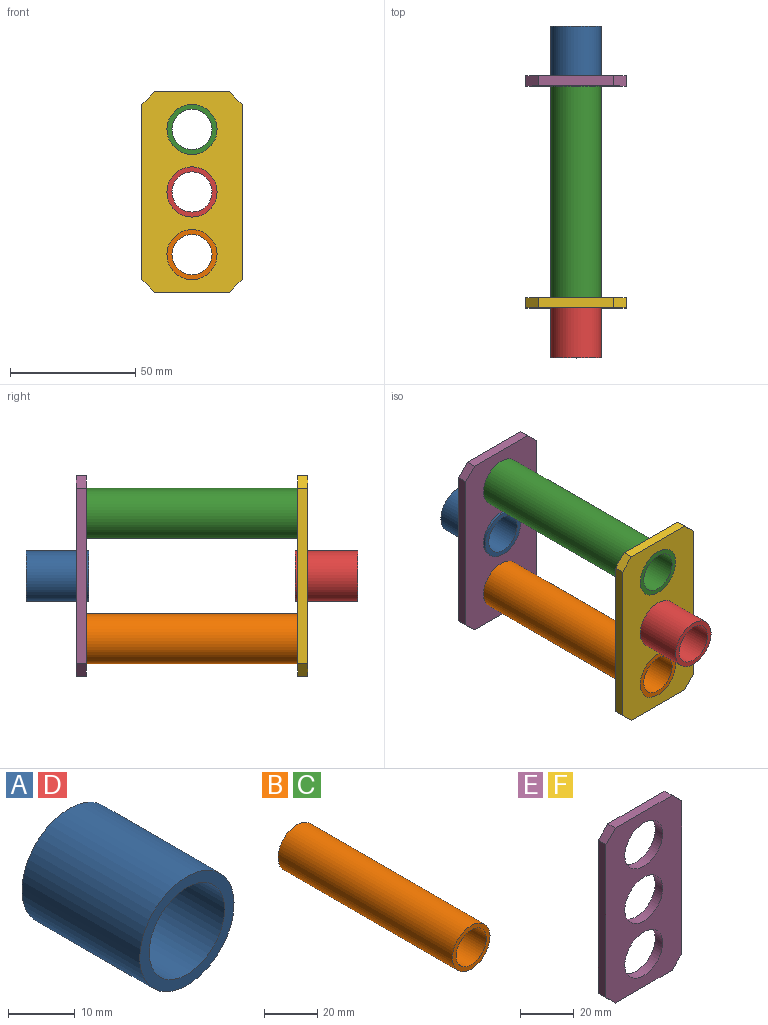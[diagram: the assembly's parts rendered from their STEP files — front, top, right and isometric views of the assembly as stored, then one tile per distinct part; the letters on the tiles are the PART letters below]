
ASSEMBLY  parts=6 mates=8
PART A: 4 faces, bbox 20x25x20 mm
  f0: cylinder r=8mm len=25mm, axis (0,1,0), area 1256.6mm2, adj f2,f3
  f1: cylinder r=10mm len=25mm, axis (0,1,0), area 1570.8mm2, adj f2,f3
  f2: plane 20x20mm, normal (0,-1,0), area 113.1mm2, adj f0,f1
  f3: plane 20x20mm, normal (0,1,0), area 113.1mm2, adj f0,f1
PART B: 4 faces, bbox 20x92.5x20 mm
  f0: cylinder r=8mm len=92.5mm, axis (0,1,0), area 4649.6mm2, adj f2,f3
  f1: cylinder r=10mm len=92.5mm, axis (0,1,0), area 5811.9mm2, adj f2,f3
  f2: plane 20x20mm, normal (0,-1,0), area 113.1mm2, adj f0,f1
  f3: plane 20x20mm, normal (0,1,0), area 113.1mm2, adj f0,f1
PART C: same geometry as B
PART D: same geometry as A
PART E: 13 faces, bbox 40x4x80 mm
  f0: plane 30x4mm, normal (0,0,1), area 120mm2, adj f4,f5,f6,f9
  f1: plane 70x4mm, normal (-1,0,0), area 280mm2, adj f4,f5,f6,f7
  f2: plane 30x4mm, normal (0,0,-1), area 120mm2, adj f4,f5,f7,f8
  f3: plane 70x4mm, normal (1,0,0), area 280mm2, adj f4,f5,f8,f9
  f4: plane 80x40mm, normal (0,-1,0), area 2207.5mm2, adj f0,f1,f2,f3,f6,f7,f8,f9
  f5: plane 80x40mm, normal (0,1,0), area 2207.5mm2, adj f0,f1,f2,f3,f6,f7,f8,f9
  f6: plane 5x5mm, normal (-0.71,0,0.71), area 28.3mm2, adj f0,f1,f4,f5
  f7: plane 5x5mm, normal (-0.71,0,-0.71), area 28.3mm2, adj f1,f2,f4,f5
  f8: plane 5x5mm, normal (0.71,0,-0.71), area 28.3mm2, adj f2,f3,f4,f5
  f9: plane 5x5mm, normal (0.71,0,0.71), area 28.3mm2, adj f0,f3,f4,f5
  f10: cylinder r=10mm len=20mm, axis (0,-1,0), area 251.3mm2, adj f4,f5
  f11: cylinder r=10mm len=20mm, axis (0,-1,0), area 251.3mm2, adj f4,f5
  f12: cylinder r=10mm len=20mm, axis (0,-1,0), area 251.3mm2, adj f4,f5
PART F: same geometry as E
PLACE A t=(-70.44,-0.5,9.48)mm
PLACE B t=(-146.73,-20.5,-26.68)mm
PLACE C t=(-146.73,-20.5,23.32)mm
PLACE D rot(axis=(-0.08,0,-1),0deg) t=(-70.44,-108,9.48)mm
PLACE E t=(-126.29,-20.5,79.54)mm
PLACE F t=(-126.29,-109,79.54)mm
MATE fastened D.f0 <-> F.f11  axis (0,1,0) through (-106.29,-108,39.54)mm
MATE fastened E.f12 <-> B.f0  axis (0,1,0) through (-106.29,-20.5,14.54)mm
MATE fastened E.f10 <-> C.f0  axis (0,1,0) through (-106.29,-20.5,64.54)mm
MATE fastened C.f0 <-> F.f10  axis (0,-1,0) through (-106.29,-113,64.54)mm
MATE cylindrical C.f0 <-> E.f10  axis (0,1,0) through (-106.29,-20.5,64.54)mm
MATE cylindrical E.f12 <-> B.f0  axis (0,1,0) through (-106.29,-20.5,14.54)mm
MATE fastened A.f0 <-> E.f11  axis (0,-1,0) through (-106.29,-25.5,39.54)mm
MATE fastened F.f12 <-> F.f12  axis (0,-1,0) through (-106.29,-113,14.54)mm
